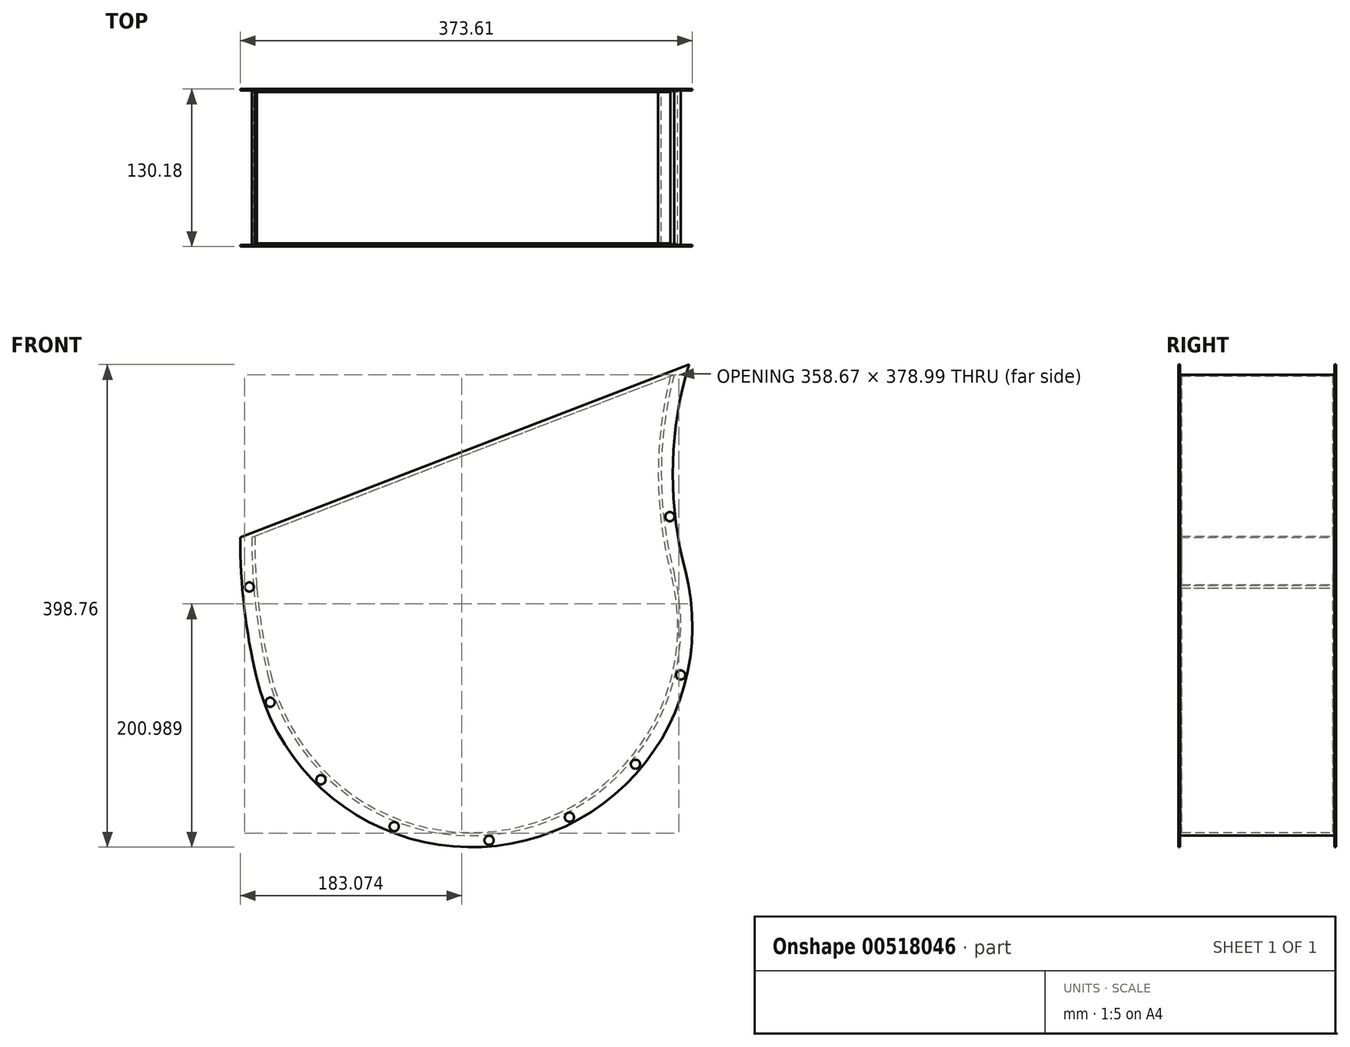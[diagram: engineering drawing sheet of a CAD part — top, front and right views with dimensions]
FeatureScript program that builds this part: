
annotation { "Feature Type Name" : "Feature", "Feature Type Description" : "" }
export const myFeature = defineFeature(function(context is Context, id is Id, definition is map)
    precondition{}
    {
        {
            var Q0;
            Q0=qCreatedBy(makeId("Front.planeOp"),FACE);
            var sketch = newSketch(context, id + "F0", { "sketchPlane" : qUnion([Q0])});
            skArc(sketch, "E0", {"start": v(-168.5, -39.37) * mm, "mid": v(41.75, -167.32) * mm, "end": v(167.24, 44.4) * mm});
            skArc(sketch, "E1", {"start": v(167.24, 44.4) * mm, "mid": v(156.68, 126.45) * mm, "end": v(167.24, 208.5) * mm});
            skArc(sketch, "E2", {"start": v(-168.5, -39.37) * mm, "mid": v(-178.42, 16.98) * mm, "end": v(-181.67, 74.1) * mm});
            skLineSegment(sketch, "E3", {"start": v(-181.67, 74.1) * mm, "end": v(167.24, 208.5) * mm});
            skArc(sketch, "E4.0", {"start": v(-177.77, -41.57) * mm, "mid": v(-187.88, 15.88) * mm, "end": v(-191.2, 74.12) * mm});
            skArc(sketch, "E4.1", {"start": v(-177.77, -41.57) * mm, "mid": v(44.05, -176.56) * mm, "end": v(176.46, 46.81) * mm});
            skArc(sketch, "E4.2", {"start": v(176.46, 46.81) * mm, "mid": v(166.2, 126.45) * mm, "end": v(176.46, 206.08) * mm});
            skArc(sketch, "E5", {"start": v(176.46, 206.08) * mm, "mid": v(177.97, 211.45) * mm, "end": v(179.67, 216.77) * mm});
            skLineSegment(sketch, "E6", {"start": v(-191.2, 74.12) * mm, "end": v(179.67, 216.77) * mm});
            skCircle(sketch, "E7", {"center": v(-166.42, -62.23) * mm, "radius": 3.81 * mm});
            skCircle(sketch, "E8", {"center": v(-124.5, -126.3) * mm, "radius": 3.81 * mm});
            skCircle(sketch, "E9", {"center": v(-63.98, -164.93) * mm, "radius": 3.81 * mm});
            skCircle(sketch, "E10", {"center": v(14.36, -176.3) * mm, "radius": 3.81 * mm});
            skCircle(sketch, "E11", {"center": v(80.82, -157.23) * mm, "radius": 3.81 * mm});
            skCircle(sketch, "E12", {"center": v(135.35, -113.46) * mm, "radius": 3.81 * mm});
            skCircle(sketch, "E13", {"center": v(172.67, -39.75) * mm, "radius": 3.81 * mm});
            skCircle(sketch, "E14", {"center": v(163.72, 91.12) * mm, "radius": 3.81 * mm});
            skCircle(sketch, "E15", {"center": v(-183.66, 33.02) * mm, "radius": 3.81 * mm});
            skSolve(sketch);
        }
        {
            var Q0;
            Q0=makeQuery(id+"F0.imprint","IMPRINT",FACE,{"disambiguationData":[TD([[makeQuery(id+"F0.imprint","IMPRINT",EDGE,{"derivedFrom":sQuery(id+"F0.wireOp",EDGE,"E0")}),1.0]])]});
            extrude(context, id + "F1", {"entities" : qUnion([Q0]), "depth" : 130.17 * mm});
        }
        {
            var Q0;
            Q0=makeQuery(id+"F1.opExtrude","SWEPT_FACE",FACE,{"disambiguationData":[OSD([sQuery(id+"F0.wireOp",EDGE,"E3")])]});
            shell(context, id + "F2", {"entities" : qUnion([Q0]), "thickness" : 2.54 * mm});
        }
        {
            var Q0;
            Q0=qSketchRegion(id+"F0",true);
            extrude(context, id + "F3", {"entities" : qUnion([Q0]), "operationType" : NewBodyOperationType.ADD, "depth" : 1.27 * mm});
        }
        {
            var Q0;
            Q0=qCreatedBy(makeId("Front.planeOp"),FACE);
            cPlane(context, id + "F4", {"entities" : qUnion([Q0]), "cplaneType" : CPlaneType.OFFSET, "offset" : 65.1 * mm, "width" : 152.4 * mm, "height" : 152.4 * mm});
        }
        {
            var Q0;
            Q0=makeQuery(id+"F1.opExtrude","SWEPT_BODY",BODY,{"disambiguationData":[OSD([sQuery(id+"F0.wireOp",EDGE,"E0"),sQuery(id+"F0.wireOp",EDGE,"E1"),sQuery(id+"F0.wireOp",EDGE,"E2"),sQuery(id+"F0.wireOp",EDGE,"E3")])]});
            var Q1;
            Q1=qCreatedBy(id+"F4.planeOp",FACE);
            mirror(context, id + "F5", {"operationType" : NewBodyOperationType.ADD, "entities" : qUnion([Q0]), "mirrorPlane" : qUnion([Q1])});
        }
    });
